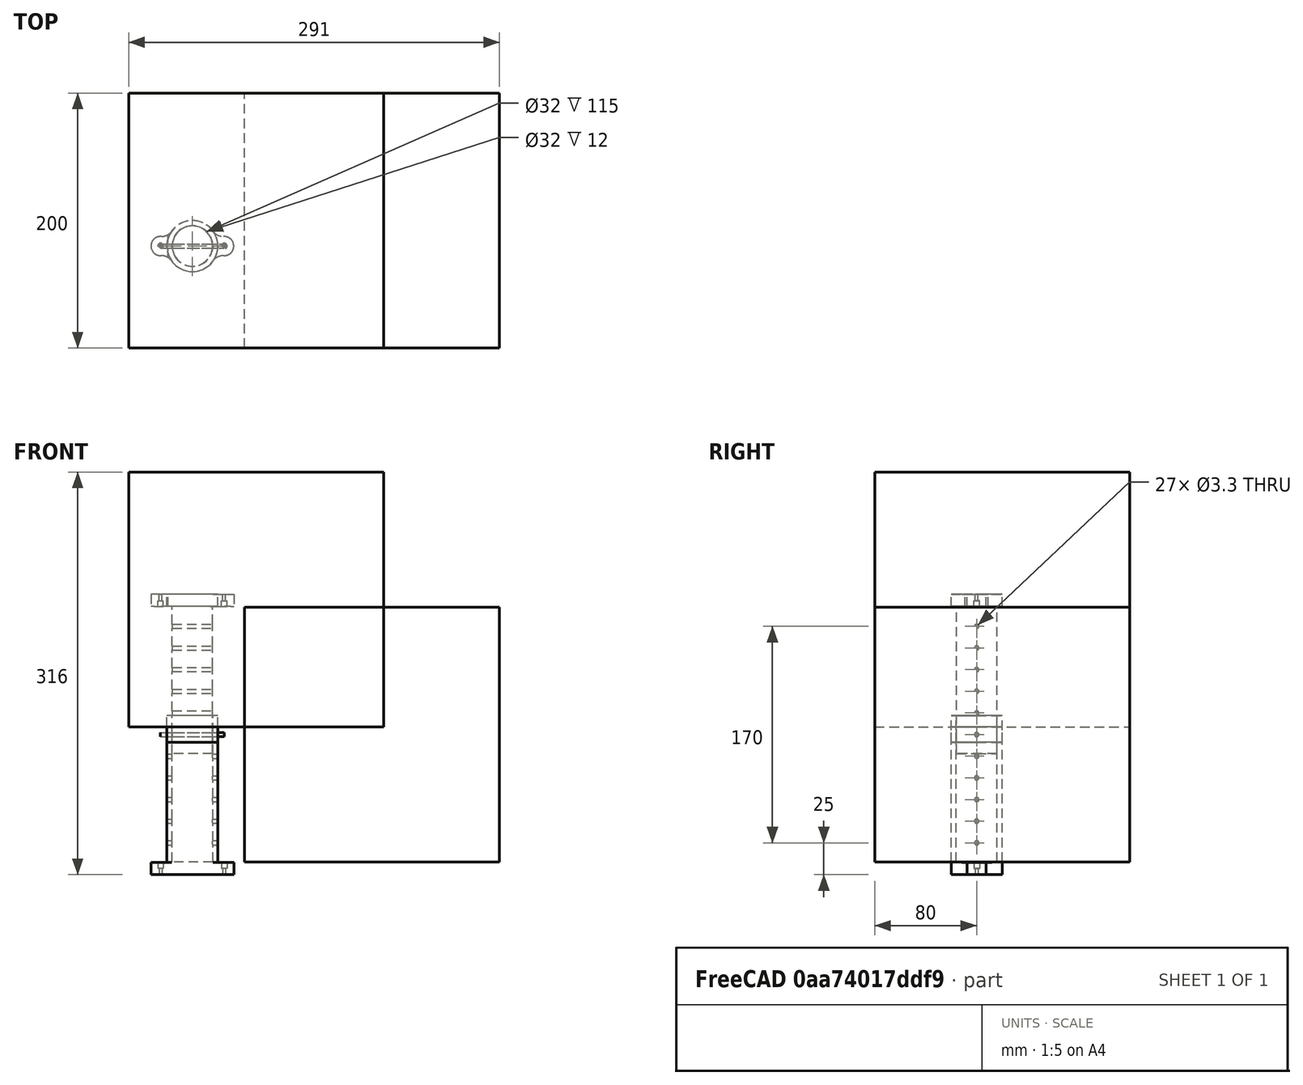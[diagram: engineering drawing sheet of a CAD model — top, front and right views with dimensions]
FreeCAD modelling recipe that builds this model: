
FCSTD DOCUMENT  (FreeCAD 0.18R4 (GitTag))
Label: patas_escritorio
License: All rights reserved
LicenseURL: http://en.wikipedia.org/wiki/All_rights_reserved
objects: Part::Cylinder×28, Part::Cut×24, Part::Box×11, Part::MultiFuse×8, Sketcher::SketchObject×8, PartDesign::Hole×8, Mesh::Feature×5, Part::FeaturePython×4, Part::Feature×3, PartDesign::Pad×2, PartDesign::Body×2, Part::Fillet×2, App::DocumentObjectGroup×2
note: 110 computed .brp shape members not serialized (recipe doc carries the construction recipe); baked Part::Feature solids carry a one-line shape summary decoded from their .brp

FEATURE [Part::Cylinder] Cylinder  label="cilindro_externo"
  Angle = 360
  AttacherType = Attacher::AttachEngine3D
  Height = 115
  Radius = 20
FEATURE [Part::Cylinder] Cylinder001  label="hueco_externo"
  Angle = 360
  AttacherType = Attacher::AttachEngine3D
  Height = 115
  Radius = 16
FEATURE [Part::Cylinder] Cylinder002  label="vastago_interno"
  Angle = 360
  AttacherType = Attacher::AttachEngine3D
  Height = 115
  Radius = 15.8
FEATURE [Part::Cut] Cut
  Base = -> Cylinder
  Refine = true
  Tool = -> Cylinder001
FEATURE [Part::Cylinder] Cylinder003
  Angle = 360
  AttacherType = Attacher::AttachEngine3D
  Height = 10
  Placement = pos=(0,0,-10) rot=(0,0,1;0rad)
  Radius = 20
FEATURE [Part::MultiFuse] Fusion  label="exterior_inferior"
  Refine = true
  Shapes = -> [Cut,Cylinder003]
FEATURE [Part::Cylinder] Cylinder004
  Angle = 360
  AttacherType = Attacher::AttachEngine3D
  Height = 10
  Placement = pos=(0,0,115) rot=(0,0,1;0rad)
  Radius = 20
FEATURE [Part::MultiFuse] Fusion001  label="interior_superior"
  Refine = true
  Shapes = -> [Cylinder002,Cylinder004]
FEATURE [Part::Cylinder] Cylinder005  label="Cylinder"
  Angle = 360
  AttacherType = Attacher::AttachEngine3D
  Height = 50
  Placement = pos=(-25,0,15) rot=(0,1,0;1.5708rad)
  Radius = 1.65
FEATURE [Part::Cylinder] Cylinder006  label="Cylinder005"
  Angle = 360
  AttacherType = Attacher::AttachEngine3D
  Height = 50
  Placement = pos=(-25,0,15) rot=(0,1,0;1.5708rad)
  Radius = 1.65
FEATURE [Part::Cut] Cut001
  Base = -> Fusion
  Refine = true
  Tool = -> Cylinder005
FEATURE [Part::Cylinder] Cylinder007  label="Cylinder006"
  Angle = 360
  AttacherType = Attacher::AttachEngine3D
  Height = 50
  Placement = pos=(-25,0,15) rot=(0,1,0;1.5708rad)
  Radius = 1.65
FEATURE [Part::Cylinder] Cylinder008  label="Cylinder007"
  Angle = 360
  AttacherType = Attacher::AttachEngine3D
  Height = 50
  Placement = pos=(-25,0,100) rot=(0,1,0;1.5708rad)
  Radius = 1.65
FEATURE [Part::Cylinder] Cylinder009  label="Cylinder008"
  Angle = 360
  AttacherType = Attacher::AttachEngine3D
  Height = 50
  Placement = pos=(-25,0,100) rot=(0,1,0;1.5708rad)
  Radius = 1.65
FEATURE [Part::Cut] Cut003  label="exterior_115"
  Base = -> Cut001
  Refine = true
  Tool = -> Cylinder008
FEATURE [Part::Cylinder] Cylinder010  label="Cylinder009"
  Angle = 360
  AttacherType = Attacher::AttachEngine3D
  Height = 50
  Placement = pos=(-25,0,100) rot=(0,1,0;1.5708rad)
  Radius = 1.65
FEATURE [Part::Cut] Cut004
  Base = -> Fusion001
  Refine = true
  Tool = -> Cylinder009
FEATURE [Part::Cut] Cut005  label="interior_sin_rebaja_115"
  Base = -> Cut004
  Placement = pos=(0,0,85) rot=(0,0,1;0rad)
  Refine = true
  Tool = -> Cylinder006
FEATURE [Part::FeaturePython] Array  # Draft array (typed FeaturePython)
  Angle = 360
  ArrayType = 0
  Axis = (0,0,1)
  Base = -> Cylinder007
  Center = (0,0,0)
  Fuse = false
  IntervalAxis = (0,0,0)
  IntervalX = (1,0,0)
  IntervalY = (0,1,0)
  IntervalZ = (0,0,17)
  NumberPolar = 1
  NumberX = 1
  NumberY = 1
  NumberZ = 6
FEATURE [Part::Cylinder] Cylinder011  label="Cylinder010"
  Angle = 360
  AttacherType = Attacher::AttachEngine3D
  Height = 50
  Placement = pos=(-25,0,15) rot=(0,1,0;1.5708rad)
  Radius = 1.65
FEATURE [Part::FeaturePython] Array001  # Draft array (typed FeaturePython)
  Angle = 360
  ArrayType = 0
  Axis = (0,0,1)
  Base = -> Cylinder011
  Center = (0,0,0)
  Fuse = false
  IntervalAxis = (0,0,0)
  IntervalX = (1,0,0)
  IntervalY = (0,1,0)
  IntervalZ = (0,0,17)
  NumberPolar = 1
  NumberX = 1
  NumberY = 1
  NumberZ = 6
  Placement = pos=(0,0,85) rot=(0,0,1;0rad)
FEATURE [Part::Cut] Cut006  label="exterior"
  Base = -> Cut003
  Refine = true
  Tool = -> Array
FEATURE [Part::Cut] Cut007
  Base = -> Cut005
  Refine = true
  Tool = -> Array001
FEATURE [Part::Cylinder] Cylinder012  label="Cylinder011"
  Angle = 360
  AttacherType = Attacher::AttachEngine3D
  Height = 10
  Radius = 15.8
FEATURE [Part::Cylinder] Cylinder013  label="Cylinder012"
  Angle = 360
  AttacherType = Attacher::AttachEngine3D
  Height = 10
  Radius = 20
FEATURE [Part::Cut] Cut008
  Base = -> Cylinder013
  Placement = pos=(0,0,190.5) rot=(0,0,1;0rad)
  Refine = true
  Tool = -> Cylinder012
FEATURE [Part::Cut] Cut009  label="interior"
  Base = -> Cut007
  Refine = true
  Tool = -> Cut008
FEATURE [Sketcher::SketchObject] Sketch
  MapMode = 5
  Placement = pos=(0,0,210) rot=(0,0,1;0rad)
  Support = -> [Cut009]
  sketch-geometry (4):
    g0: ArcOfCircle CenterX=-25 CenterY=-2.4866e-12 CenterZ=0 NormalX=0 NormalY=0 NormalZ=1 AngleXU=0 Radius=7.5 StartAngle=1.5708 EndAngle=4.71239
    g1: ArcOfCircle CenterX=25 CenterY=-2.4702e-12 CenterZ=0 NormalX=0 NormalY=0 NormalZ=1 AngleXU=0 Radius=7.5 StartAngle=4.71239 EndAngle=7.85398
    g2: LineSegment StartX=-25 StartY=-7.5 StartZ=0 EndX=25 EndY=-7.5 EndZ=0
    g3: LineSegment StartX=-25 StartY=7.5 StartZ=0 EndX=25 EndY=7.5 EndZ=0
  constraints (9):
    c: Tangent(g0,g3) = 1.5708
    c: Tangent(g0,g2) = -1.5708
    c: Tangent(g2,g1) = -1.5708
    c: Tangent(g3,g1) = 1.5708
    c: Horizontal(g2)
    c: Equal(g0,g1)
    c: Symmetric(g0,g1,g-1)
    c: DistanceY(g0,g0) = 15
    c: DistanceX(g0,g1) = 50
FEATURE [PartDesign::Pad] Pad
  Length = 9.5
  Length2 = 100
  Profile = -> Sketch
  Refine = true
  Type = 0
FEATURE [Sketcher::SketchObject] Sketch001
  ExternalGeometry = -> [Pad]
  MapMode = 5
  Placement = pos=(0,0,210) rot=(1,0,0;3.14159rad)
  Support = -> [Pad]
  sketch-geometry (1):
    g0: Circle CenterX=-25 CenterY=0 CenterZ=0 NormalX=0 NormalY=0 NormalZ=1 AngleXU=0 Radius=1.33279
  constraints (2):
    c: PointOnObject(g0,g-1)
    c: Vertical(g0,g-3)
FEATURE [PartDesign::Hole] Hole
  BaseFeature = -> Pad
  Depth = 4.5
  DepthType = 0
  Diameter = 4.4
  DrillPoint = 0
  DrillPointAngle = 118
  HoleCutCountersinkAngle = 90
  HoleCutDepth = 0
  HoleCutDiameter = 4
  HoleCutType = 0
  ModelActualThread = false
  Profile = -> Pad [Face4]
  Refine = true
  Tapered = false
  TaperedAngle = 90
  ThreadAngle = 0
  ThreadClass = 0
  ThreadCutOffInner = 0
  ThreadCutOffOuter = 0
  ThreadDirection = 0
  ThreadFit = 0
  ThreadPitch = 0
  ThreadSize = 5
  ThreadType = 1
  Threaded = false
FEATURE [Sketcher::SketchObject] CopySketch002
  Placement = pos=(0,0,210) rot=(1,0,0;3.14159rad)
  sketch-geometry (1):
    g0: Circle CenterX=25 CenterY=0 CenterZ=0 NormalX=0 NormalY=0 NormalZ=1 AngleXU=0 Radius=0.857888
  constraints (1):
    c: PointOnObject(g0,g-1)
FEATURE [PartDesign::Hole] Hole001
  BaseFeature = -> Hole
  Depth = 4.5
  DepthType = 0
  Diameter = 4.4
  DrillPoint = 0
  DrillPointAngle = 118
  HoleCutCountersinkAngle = 90
  HoleCutDepth = 0
  HoleCutDiameter = 4
  HoleCutType = 0
  ModelActualThread = false
  Profile = -> CopySketch002
  Refine = true
  Tapered = false
  TaperedAngle = 90
  ThreadAngle = 60
  ThreadClass = 0
  ThreadCutOffInner = 0.0378886
  ThreadCutOffOuter = 0.0757772
  ThreadDirection = 0
  ThreadFit = 0
  ThreadPitch = 0.35
  ThreadSize = 5
  ThreadType = 1
  Threaded = false
FEATURE [Sketcher::SketchObject] CopySketch002001  label="CopySketch003"
  Placement = pos=(0,0,210) rot=(1,0,0;3.14159rad)
  sketch-geometry (1):
    g0: Circle CenterX=25 CenterY=0 CenterZ=0 NormalX=0 NormalY=0 NormalZ=1 AngleXU=0 Radius=0.857888
  constraints (1):
    c: PointOnObject(g0,g-1)
FEATURE [PartDesign::Hole] Hole002
  BaseFeature = -> Hole001
  Depth = 25
  DepthType = 1
  Diameter = 2.2
  DrillPoint = 0
  DrillPointAngle = 118
  HoleCutCountersinkAngle = 90
  HoleCutDepth = 0
  HoleCutDiameter = 2
  HoleCutType = 0
  ModelActualThread = false
  Profile = -> CopySketch002001
  Refine = true
  Tapered = false
  TaperedAngle = 90
  ThreadAngle = 0
  ThreadClass = 0
  ThreadCutOffInner = 0
  ThreadCutOffOuter = 0
  ThreadDirection = 0
  ThreadFit = 0
  ThreadPitch = 0
  ThreadSize = 1
  ThreadType = 1
  Threaded = false
FEATURE [PartDesign::Hole] Hole003
  BaseFeature = -> Hole002
  Depth = 25
  DepthType = 1
  Diameter = 2.2
  DrillPoint = 0
  DrillPointAngle = 118
  HoleCutCountersinkAngle = 90
  HoleCutDepth = 0
  HoleCutDiameter = 2
  HoleCutType = 0
  ModelActualThread = false
  Profile = -> Sketch001
  Refine = true
  Tapered = false
  TaperedAngle = 90
  ThreadAngle = 0
  ThreadClass = 0
  ThreadCutOffInner = 0
  ThreadCutOffOuter = 0
  ThreadDirection = 0
  ThreadFit = 0
  ThreadPitch = 0
  ThreadSize = 1
  ThreadType = 1
  Threaded = false
FEATURE [PartDesign::Body] Body
  Group = -> [Sketch,Pad,Hole,Hole001,Hole002,Hole003]
  Origin = -> Origin
  Tip = -> Hole003
FEATURE [Part::Cylinder] Cylinder014  label="vastago_interno001"
  Angle = 360
  AttacherType = Attacher::AttachEngine3D
  Height = 115
  Radius = 15.8
FEATURE [Part::Cylinder] Cylinder015  label="Cylinder013"
  Angle = 360
  AttacherType = Attacher::AttachEngine3D
  Height = 50
  Placement = pos=(-25,0,100) rot=(0,1,0;1.5708rad)
  Radius = 1.65
FEATURE [Part::Cylinder] Cylinder016  label="Cylinder014"
  Angle = 360
  AttacherType = Attacher::AttachEngine3D
  Height = 50
  Placement = pos=(-25,0,15) rot=(0,1,0;1.5708rad)
  Radius = 1.65
FEATURE [Part::FeaturePython] Array002  # Draft array (typed FeaturePython)
  Angle = 360
  ArrayType = 0
  Axis = (0,0,1)
  Base = -> Cylinder016
  Center = (0,0,0)
  Fuse = false
  IntervalAxis = (0,0,0)
  IntervalX = (1,0,0)
  IntervalY = (0,1,0)
  IntervalZ = (0,0,17)
  NumberPolar = 1
  NumberX = 1
  NumberY = 1
  NumberZ = 6
  Placement = pos=(0,0,85) rot=(0,0,1;0rad)
FEATURE [Part::Cylinder] Cylinder017  label="Cylinder016"
  Angle = 360
  AttacherType = Attacher::AttachEngine3D
  Height = 10
  Radius = 15.8
FEATURE [Part::Cylinder] Cylinder018  label="Cylinder017"
  Angle = 360
  AttacherType = Attacher::AttachEngine3D
  Height = 10
  Radius = 20
FEATURE [Part::Cylinder] Cylinder019
  Angle = 360
  AttacherType = Attacher::AttachEngine3D
  Height = 10
  Placement = pos=(0,0,115) rot=(0,0,1;0rad)
  Radius = 20
FEATURE [Part::MultiFuse] Fusion002  label="interior_superior001"
  Refine = true
  Shapes = -> [Cylinder014,Cylinder019]
FEATURE [Part::Cylinder] Cylinder020
  Angle = 360
  AttacherType = Attacher::AttachEngine3D
  Height = 50
  Placement = pos=(-25,0,15) rot=(0,1,0;1.5708rad)
  Radius = 1.65
FEATURE [Part::Cut] Cut012
  Base = -> Cylinder018
  Placement = pos=(0,0,190.5) rot=(0,0,1;0rad)
  Refine = true
  Tool = -> Cylinder017
FEATURE [Part::Cut] Cut013
  Base = -> Fusion002
  Refine = true
  Tool = -> Cylinder015
FEATURE [Part::Cut] Cut014  label="interior_sin_rebaja_116"
  Base = -> Cut013
  Placement = pos=(0,0,85) rot=(0,0,1;0rad)
  Refine = true
  Tool = -> Cylinder020
FEATURE [Part::Cut] Cut010
  Base = -> Cut014
  Refine = true
  Tool = -> Array002
FEATURE [Part::Cut] Cut011
  Base = -> Cut010
  Refine = true
  Tool = -> Cut012
FEATURE [Part::Box] Box  label="Cube"
  AttacherType = Attacher::AttachEngine3D
  Height = 200
  Length = 60
  Placement = pos=(-30,-30,10) rot=(0,0,1;0rad)
  Width = 60
FEATURE [Part::Cut] Cut015  label="pestania1"
  Base = -> Body
  Placement = pos=(0,0,-9.5) rot=(0,0,1;0rad)
  Refine = true
  Tool = -> Box
FEATURE [Part::Cylinder] Cylinder021  label="vastago_interno002"
  Angle = 360
  AttacherType = Attacher::AttachEngine3D
  Height = 115
  Radius = 15.8
FEATURE [Part::Cylinder] Cylinder022  label="Cylinder021"
  Angle = 360
  AttacherType = Attacher::AttachEngine3D
  Height = 50
  Placement = pos=(-25,0,100) rot=(0,1,0;1.5708rad)
  Radius = 1.65
FEATURE [Part::Cylinder] Cylinder023  label="Cylinder022"
  Angle = 360
  AttacherType = Attacher::AttachEngine3D
  Height = 50
  Placement = pos=(-25,0,15) rot=(0,1,0;1.5708rad)
  Radius = 1.65
FEATURE [Part::FeaturePython] Array003  # Draft array (typed FeaturePython)
  Angle = 360
  ArrayType = 0
  Axis = (0,0,1)
  Base = -> Cylinder023
  Center = (0,0,0)
  Fuse = false
  IntervalAxis = (0,0,0)
  IntervalX = (1,0,0)
  IntervalY = (0,1,0)
  IntervalZ = (0,0,17)
  NumberPolar = 1
  NumberX = 1
  NumberY = 1
  NumberZ = 6
  Placement = pos=(0,0,85) rot=(0,0,1;0rad)
FEATURE [Part::Cylinder] Cylinder024  label="Cylinder023"
  Angle = 360
  AttacherType = Attacher::AttachEngine3D
  Height = 10
  Radius = 15.8
FEATURE [Part::Cylinder] Cylinder025  label="Cylinder024"
  Angle = 360
  AttacherType = Attacher::AttachEngine3D
  Height = 10
  Radius = 20
FEATURE [Part::Cylinder] Cylinder026
  Angle = 360
  AttacherType = Attacher::AttachEngine3D
  Height = 10
  Placement = pos=(0,0,115) rot=(0,0,1;0rad)
  Radius = 20
FEATURE [Part::MultiFuse] Fusion003  label="interior_superior002"
  Refine = true
  Shapes = -> [Cylinder021,Cylinder026]
FEATURE [Part::Cylinder] Cylinder027
  Angle = 360
  AttacherType = Attacher::AttachEngine3D
  Height = 50
  Placement = pos=(-25,0,15) rot=(0,1,0;1.5708rad)
  Radius = 1.65
FEATURE [Part::Cut] Cut018
  Base = -> Cylinder025
  Placement = pos=(0,0,190.5) rot=(0,0,1;0rad)
  Refine = true
  Tool = -> Cylinder024
FEATURE [Part::Cut] Cut019
  Base = -> Fusion003
  Refine = true
  Tool = -> Cylinder022
FEATURE [Part::Cut] Cut020  label="interior_sin_rebaja_117"
  Base = -> Cut019
  Placement = pos=(0,0,85) rot=(0,0,1;0rad)
  Refine = true
  Tool = -> Cylinder027
FEATURE [Part::Cut] Cut016
  Base = -> Cut020
  Refine = true
  Tool = -> Array003
FEATURE [Part::Cut] Cut017  label="interior001"
  Base = -> Cut016
  Refine = true
  Tool = -> Cut018
FEATURE [Part::Box] Box001  label="Cube001"
  AttacherType = Attacher::AttachEngine3D
  Height = 200
  Length = 60
  Placement = pos=(-30,-30,10) rot=(0,0,1;0rad)
  Width = 60
FEATURE [Sketcher::SketchObject] Sketch002
  MapMode = 5
  Placement = pos=(0,0,210) rot=(0,0,1;0rad)
  Support = -> [Cut017]
  sketch-geometry (4):
    g0: ArcOfCircle CenterX=-25 CenterY=-2.4866e-12 CenterZ=0 NormalX=0 NormalY=0 NormalZ=1 AngleXU=0 Radius=7.5 StartAngle=1.5708 EndAngle=4.71239
    g1: ArcOfCircle CenterX=25 CenterY=-2.4702e-12 CenterZ=0 NormalX=0 NormalY=0 NormalZ=1 AngleXU=0 Radius=7.5 StartAngle=4.71239 EndAngle=7.85398
    g2: LineSegment StartX=-25 StartY=-7.5 StartZ=0 EndX=25 EndY=-7.5 EndZ=0
    g3: LineSegment StartX=-25 StartY=7.5 StartZ=0 EndX=25 EndY=7.5 EndZ=0
  constraints (9):
    c: Tangent(g0,g3) = 1.5708
    c: Tangent(g0,g2) = -1.5708
    c: Tangent(g2,g1) = -1.5708
    c: Tangent(g3,g1) = 1.5708
    c: Horizontal(g2)
    c: Equal(g0,g1)
    c: Symmetric(g0,g1,g-1)
    c: DistanceY(g0,g0) = 15
    c: DistanceX(g0,g1) = 50
FEATURE [PartDesign::Pad] Pad001
  Length = 9.5
  Length2 = 100
  Profile = -> Sketch002
  Refine = true
  Type = 0
FEATURE [PartDesign::Hole] Hole006
  BaseFeature = -> Pad001
  Depth = 4.5
  DepthType = 0
  Diameter = 4.4
  DrillPoint = 0
  DrillPointAngle = 118
  HoleCutCountersinkAngle = 90
  HoleCutDepth = 0
  HoleCutDiameter = 4
  HoleCutType = 0
  ModelActualThread = false
  Profile = -> Pad001 [Face4]
  Refine = true
  Tapered = false
  TaperedAngle = 90
  ThreadAngle = 0
  ThreadClass = 0
  ThreadCutOffInner = 0
  ThreadCutOffOuter = 0
  ThreadDirection = 0
  ThreadFit = 0
  ThreadPitch = 0
  ThreadSize = 5
  ThreadType = 1
  Threaded = false
FEATURE [Sketcher::SketchObject] Sketch003
  ExternalGeometry = -> [Pad001]
  MapMode = 5
  Placement = pos=(0,0,210) rot=(1,0,0;3.14159rad)
  Support = -> [Pad001]
  sketch-geometry (1):
    g0: Circle CenterX=-25 CenterY=0 CenterZ=0 NormalX=0 NormalY=0 NormalZ=1 AngleXU=0 Radius=1.33279
  constraints (2):
    c: PointOnObject(g0,g-1)
    c: Vertical(g0,g-3)
FEATURE [Sketcher::SketchObject] CopySketch002002  label="CopySketch004"
  Placement = pos=(0,0,210) rot=(1,0,0;3.14159rad)
  sketch-geometry (1):
    g0: Circle CenterX=25 CenterY=0 CenterZ=0 NormalX=0 NormalY=0 NormalZ=1 AngleXU=0 Radius=0.857888
  constraints (1):
    c: PointOnObject(g0,g-1)
FEATURE [Sketcher::SketchObject] CopySketch002003
  Placement = pos=(0,0,210) rot=(1,0,0;3.14159rad)
  sketch-geometry (1):
    g0: Circle CenterX=25 CenterY=0 CenterZ=0 NormalX=0 NormalY=0 NormalZ=1 AngleXU=0 Radius=0.857888
  constraints (1):
    c: PointOnObject(g0,g-1)
FEATURE [PartDesign::Hole] Hole007
  BaseFeature = -> Hole006
  Depth = 4.5
  DepthType = 0
  Diameter = 4.4
  DrillPoint = 0
  DrillPointAngle = 118
  HoleCutCountersinkAngle = 90
  HoleCutDepth = 0
  HoleCutDiameter = 4
  HoleCutType = 0
  ModelActualThread = false
  Profile = -> CopySketch002003
  Refine = true
  Tapered = false
  TaperedAngle = 90
  ThreadAngle = 60
  ThreadClass = 0
  ThreadCutOffInner = 0.0378886
  ThreadCutOffOuter = 0.0757772
  ThreadDirection = 0
  ThreadFit = 0
  ThreadPitch = 0.35
  ThreadSize = 5
  ThreadType = 1
  Threaded = false
FEATURE [PartDesign::Hole] Hole005
  BaseFeature = -> Hole007
  Depth = 25
  DepthType = 1
  Diameter = 2.2
  DrillPoint = 0
  DrillPointAngle = 118
  HoleCutCountersinkAngle = 90
  HoleCutDepth = 0
  HoleCutDiameter = 2
  HoleCutType = 0
  ModelActualThread = false
  Profile = -> CopySketch002002
  Refine = true
  Tapered = false
  TaperedAngle = 90
  ThreadAngle = 0
  ThreadClass = 0
  ThreadCutOffInner = 0
  ThreadCutOffOuter = 0
  ThreadDirection = 0
  ThreadFit = 0
  ThreadPitch = 0
  ThreadSize = 1
  ThreadType = 1
  Threaded = false
FEATURE [PartDesign::Hole] Hole004
  BaseFeature = -> Hole005
  Depth = 25
  DepthType = 1
  Diameter = 2.2
  DrillPoint = 0
  DrillPointAngle = 118
  HoleCutCountersinkAngle = 90
  HoleCutDepth = 0
  HoleCutDiameter = 2
  HoleCutType = 0
  ModelActualThread = false
  Profile = -> Sketch003
  Refine = true
  Tapered = false
  TaperedAngle = 90
  ThreadAngle = 0
  ThreadClass = 0
  ThreadCutOffInner = 0
  ThreadCutOffOuter = 0
  ThreadDirection = 0
  ThreadFit = 0
  ThreadPitch = 0
  ThreadSize = 1
  ThreadType = 1
  Threaded = false
FEATURE [PartDesign::Body] Body001
  Group = -> [Sketch002,Pad001,Hole006,Hole007,Hole005,Hole004]
  Origin = -> Origin001
  Tip = -> Hole004
FEATURE [Part::Cut] Cut021  label="pestania2"
  Base = -> Body001
  Placement = pos=(0,0,209.5) rot=(0,1,0;3.14159rad)
  Refine = true
  Tool = -> Box001
FEATURE [Part::MultiFuse] Fusion004
  Refine = true
  Shapes = -> [Cut006,Cut021]
FEATURE [Part::Fillet] Fillet  label="pata_exterior"
  Base = -> Fusion004
  Edges = 4 edges r=10: [Edge2,Edge11,Edge15,Edge17]
FEATURE [Part::MultiFuse] Fusion005
  Refine = true
  Shapes = -> [Cut009,Cut015]
FEATURE [Part::Fillet] Fillet001  label="pata_interior"
  Base = -> Fusion005
  Edges = 4 edges r=10: [Edge1,Edge3,Edge9,Edge11]
FEATURE [Part::Feature] Fillet002  label="pata_exterior001"
  shape: bbox 65 x 40 x 125 mm, 35 faces (baked)
FEATURE [Part::Feature] Fillet001001  label="pata_interior001"
  shape: bbox 65 x 40 x 125 mm, 28 faces (baked)
FEATURE [Part::Box] Box002  label="Cube002"
  AttacherType = Attacher::AttachEngine3D
  Height = 200
  Length = 200
  Placement = pos=(41,-80,0) rot=(0,0,1;0rad)
  Width = 200
FEATURE [Part::Box] Box003  label="Cube003"
  AttacherType = Attacher::AttachEngine3D
  Height = 200
  Length = 200
  Placement = pos=(-50,-80,-106) rot=(0,0,1;0rad)
  Width = 200
FEATURE [Part::Box] Box004  label="Cube004"
  AttacherType = Attacher::AttachEngine3D
  Height = 200
  Length = 200
  Placement = pos=(-50,-80,106) rot=(0,0,1;0rad)
  Width = 200
FEATURE [Part::MultiFuse] Fusion006
  Refine = true
  Shapes = -> [Box002,Box004,Box003]
FEATURE [Part::Box] Box005  label="Cube005"
  AttacherType = Attacher::AttachEngine3D
  Height = 200
  Length = 200
  Placement = pos=(41,-80,0) rot=(0,0,1;0rad)
  Width = 200
FEATURE [Part::Box] Box006  label="Cube006"
  AttacherType = Attacher::AttachEngine3D
  Height = 200
  Length = 200
  Placement = pos=(-50,-80,106) rot=(0,0,1;0rad)
  Width = 200
FEATURE [Part::Box] Box007  label="Cube007"
  AttacherType = Attacher::AttachEngine3D
  Height = 200
  Length = 200
  Placement = pos=(-50,-80,-106) rot=(0,0,1;0rad)
  Width = 200
FEATURE [Part::MultiFuse] Fusion007
  Refine = true
  Shapes = -> [Box005,Box006,Box007]
FEATURE [Part::Cut] Cut022  label="test_exterior"
  Base = -> Fillet002
  Refine = true
  Tool = -> Fusion006
FEATURE [Part::Feature] Fillet001002  label="pata_interior002"
  shape: bbox 65 x 40 x 125 mm, 28 faces (baked)
FEATURE [Part::Cut] Cut023  label="test_interior"
  Base = -> Fillet001001
  Refine = true
  Tool = -> Fusion007
FEATURE [Part::Box] Box008  label="Cube008"
  AttacherType = Attacher::AttachEngine3D
  Height = 200
  Length = 200
  Placement = pos=(41,-80,0) rot=(0,0,1;0rad)
  Width = 200
FEATURE [Part::Box] Box009  label="Cube009"
  AttacherType = Attacher::AttachEngine3D
  Height = 200
  Length = 200
  Placement = pos=(-19,-80,17) rot=(0,0,1;0rad)
  Width = 200
FEATURE [Part::Box] Box010  label="Cube010"
  AttacherType = Attacher::AttachEngine3D
  Height = 200
  Length = 200
  Placement = pos=(-50,-80,106) rot=(0,0,1;0rad)
  Width = 200
FEATURE [Part::Cut] Cut024  label="test_pestania"
  Base = -> Fillet001002
  Refine = true
  Tool = -> Box009
FEATURE [Mesh::Feature] Mesh  label="test_pestania (Meshed)"
FEATURE [Mesh::Feature] Mesh001  label="test_interior (Meshed)"
FEATURE [Mesh::Feature] Mesh002  label="test_exterior (Meshed)"
FEATURE [App::DocumentObjectGroup] Group001  label="test"
  Group = -> [Cut024,Cut023,Cut022,Mesh,Mesh001,Mesh002]
FEATURE [Mesh::Feature] Mesh003  label="pata_exterior (Meshed)"
FEATURE [Mesh::Feature] Mesh004  label="pata_interior (Meshed)"
FEATURE [App::DocumentObjectGroup] Group  label="patas"
  Group = -> [Fillet,Fillet001,Mesh004,Mesh003]
